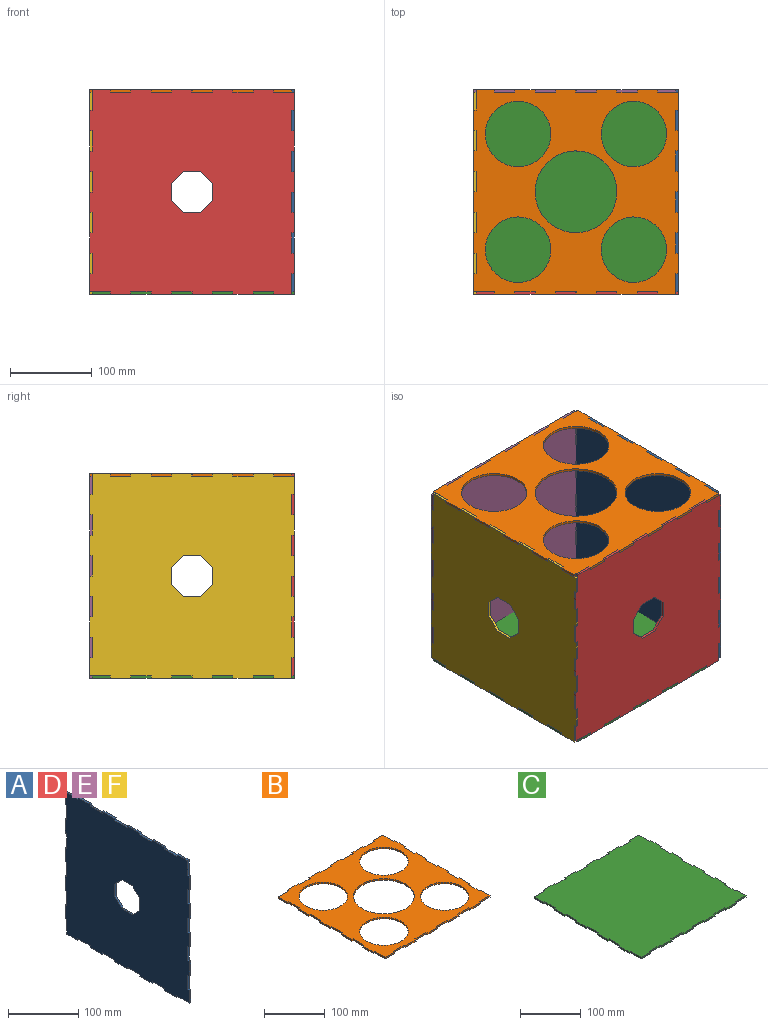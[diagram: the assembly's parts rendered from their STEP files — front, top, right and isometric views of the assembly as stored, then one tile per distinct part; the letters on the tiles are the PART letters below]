
ASSEMBLY  parts=6 mates=4
PART A: 86 faces, bbox 3x250x250 mm
  f0: plane 3x3mm, normal (0,0,1), area 9mm2, adj f1,f83,f84,f85
  f1: plane 25x3mm, normal (0,-1,0), area 75mm2, adj f0,f2,f84,f85
  f2: plane 3x3mm, normal (0,0,-1), area 9mm2, adj f1,f3,f84,f85
  f3: plane 25x3mm, normal (0,-1,0), area 75mm2, adj f2,f4,f84,f85
  f4: plane 3x3mm, normal (0,0,1), area 9mm2, adj f3,f5,f84,f85
  f5: plane 25x3mm, normal (0,-1,0), area 75mm2, adj f4,f6,f84,f85
  f6: plane 22x3mm, normal (0,0,1), area 66mm2, adj f5,f7,f84,f85
  f7: plane 3x3mm, normal (0,1,0), area 9mm2, adj f6,f8,f84,f85
  f8: plane 25x3mm, normal (0,0,1), area 75mm2, adj f7,f9,f84,f85
  f9: plane 3x3mm, normal (0,-1,0), area 9mm2, adj f8,f10,f84,f85
  f10: plane 25x3mm, normal (0,0,1), area 75mm2, adj f9,f11,f84,f85
  f11: plane 3x3mm, normal (0,1,0), area 9mm2, adj f10,f12,f84,f85
  f12: plane 25x3mm, normal (0,0,1), area 75mm2, adj f11,f13,f84,f85
  f13: plane 3x3mm, normal (0,-1,0), area 9mm2, adj f12,f14,f84,f85
  f14: plane 25x3mm, normal (0,0,1), area 75mm2, adj f13,f15,f84,f85
  f15: plane 3x3mm, normal (0,1,0), area 9mm2, adj f14,f16,f84,f85
  f16: plane 25x3mm, normal (0,0,1), area 75mm2, adj f15,f17,f84,f85
  f17: plane 3x3mm, normal (0,-1,0), area 9mm2, adj f16,f18,f84,f85
  f18: plane 25x3mm, normal (0,0,1), area 75mm2, adj f17,f19,f84,f85
  f19: plane 3x3mm, normal (0,1,0), area 9mm2, adj f18,f20,f84,f85
  f20: plane 25x3mm, normal (0,0,1), area 75mm2, adj f19,f21,f84,f85
  f21: plane 3x3mm, normal (0,-1,0), area 9mm2, adj f20,f22,f84,f85
  f22: plane 25x3mm, normal (0,0,1), area 75mm2, adj f21,f23,f84,f85
  f23: plane 3x3mm, normal (0,1,0), area 9mm2, adj f22,f24,f84,f85
  f24: plane 25x3mm, normal (0,0,1), area 75mm2, adj f23,f25,f84,f85
  f25: plane 22x3mm, normal (0,1,0), area 66mm2, adj f24,f26,f84,f85
  f26: plane 3x3mm, normal (0,0,-1), area 9mm2, adj f25,f27,f84,f85
  f27: plane 25x3mm, normal (0,1,0), area 75mm2, adj f26,f28,f84,f85
  f28: plane 3x3mm, normal (0,0,1), area 9mm2, adj f27,f29,f84,f85
  f29: plane 25x3mm, normal (0,1,0), area 75mm2, adj f28,f30,f84,f85
  f30: plane 3x3mm, normal (0,0,-1), area 9mm2, adj f29,f31,f84,f85
  f31: plane 25x3mm, normal (0,1,0), area 75mm2, adj f30,f32,f84,f85
  f32: plane 3x3mm, normal (0,0,1), area 9mm2, adj f31,f33,f84,f85
  f33: plane 25x3mm, normal (0,1,0), area 75mm2, adj f32,f34,f84,f85
  f34: plane 3x3mm, normal (0,0,-1), area 9mm2, adj f33,f35,f84,f85
  f35: plane 25x3mm, normal (0,1,0), area 75mm2, adj f34,f36,f84,f85
  f36: plane 3x3mm, normal (0,0,1), area 9mm2, adj f35,f37,f84,f85
  f37: plane 25x3mm, normal (0,1,0), area 75mm2, adj f36,f38,f84,f85
  f38: plane 3x3mm, normal (0,0,-1), area 9mm2, adj f37,f39,f84,f85
  f39: plane 25x3mm, normal (0,1,0), area 75mm2, adj f38,f40,f84,f85
  f40: plane 3x3mm, normal (0,0,1), area 9mm2, adj f39,f41,f84,f85
  f41: plane 25x3mm, normal (0,1,0), area 75mm2, adj f40,f42,f84,f85
  f42: plane 3x3mm, normal (0,0,-1), area 9mm2, adj f41,f43,f84,f85
  f43: plane 25x3mm, normal (0,1,0), area 75mm2, adj f42,f44,f84,f85
  f44: plane 22x3mm, normal (0,0,-1), area 66mm2, adj f43,f45,f84,f85
  f45: plane 3x3mm, normal (0,-1,0), area 9mm2, adj f44,f46,f84,f85
  f46: plane 25x3mm, normal (0,0,-1), area 75mm2, adj f45,f47,f84,f85
  f47: plane 3x3mm, normal (0,1,0), area 9mm2, adj f46,f48,f84,f85
  f48: plane 25x3mm, normal (0,0,-1), area 75mm2, adj f47,f49,f84,f85
  f49: plane 3x3mm, normal (0,-1,0), area 9mm2, adj f48,f50,f84,f85
  f50: plane 25x3mm, normal (0,0,-1), area 75mm2, adj f49,f51,f84,f85
  f51: plane 3x3mm, normal (0,1,0), area 9mm2, adj f50,f52,f84,f85
  f52: plane 25x3mm, normal (0,0,-1), area 75mm2, adj f51,f53,f84,f85
  f53: plane 3x3mm, normal (0,-1,0), area 9mm2, adj f52,f54,f84,f85
  f54: plane 25x3mm, normal (0,0,-1), area 75mm2, adj f53,f55,f84,f85
  f55: plane 3x3mm, normal (0,1,0), area 9mm2, adj f54,f56,f84,f85
  f56: plane 25x3mm, normal (0,0,-1), area 75mm2, adj f55,f57,f84,f85
  f57: plane 3x3mm, normal (0,-1,0), area 9mm2, adj f56,f58,f84,f85
  f58: plane 25x3mm, normal (0,0,-1), area 75mm2, adj f57,f59,f84,f85
  f59: plane 3x3mm, normal (0,1,0), area 9mm2, adj f58,f60,f84,f85
  f60: plane 25x3mm, normal (0,0,-1), area 75mm2, adj f59,f61,f84,f85
  f61: plane 3x3mm, normal (0,-1,0), area 9mm2, adj f60,f62,f84,f85
  f62: plane 25x3mm, normal (0,0,-1), area 75mm2, adj f61,f63,f84,f85
  f63: plane 22x3mm, normal (0,-1,0), area 66mm2, adj f62,f64,f84,f85
  f64: plane 3x3mm, normal (0,0,1), area 9mm2, adj f63,f65,f84,f85
  f65: plane 25x3mm, normal (0,-1,0), area 75mm2, adj f64,f66,f84,f85
  f66: plane 3x3mm, normal (0,0,-1), area 9mm2, adj f65,f67,f84,f85
  f67: plane 25x3mm, normal (0,-1,0), area 75mm2, adj f66,f68,f84,f85
  f68: plane 3x3mm, normal (0,0,1), area 9mm2, adj f67,f69,f84,f85
  f69: plane 25x3mm, normal (0,-1,0), area 75mm2, adj f68,f70,f84,f85
  f70: plane 3x3mm, normal (0,0,-1), area 9mm2, adj f69,f71,f84,f85
  f71: plane 25x3mm, normal (0,-1,0), area 75mm2, adj f70,f72,f84,f85
  f72: plane 3x3mm, normal (0,0,1), area 9mm2, adj f71,f73,f84,f85
  f73: plane 25x3mm, normal (0,-1,0), area 75mm2, adj f72,f74,f84,f85
  f74: plane 3x3mm, normal (0,0,-1), area 9mm2, adj f73,f83,f84,f85
  f75: plane 14.88x14.88mm, normal (0,-0.71,0.71), area 63.1mm2, adj f76,f82,f84,f85
  f76: plane 21.04x3mm, normal (0,-1,0), area 63.1mm2, adj f75,f77,f84,f85
  f77: plane 14.88x14.88mm, normal (0,-0.71,-0.71), area 63.1mm2, adj f76,f78,f84,f85
  f78: plane 21.04x3mm, normal (0,0,-1), area 63.1mm2, adj f77,f79,f84,f85
  f79: plane 14.88x14.88mm, normal (0,0.71,-0.71), area 63.1mm2, adj f78,f80,f84,f85
  f80: plane 21.04x3mm, normal (0,1,0), area 63.1mm2, adj f79,f81,f84,f85
  f81: plane 14.88x14.88mm, normal (0,0.71,0.71), area 63.1mm2, adj f80,f82,f84,f85
  f82: plane 21.04x3mm, normal (0,0,1), area 63.1mm2, adj f75,f81,f84,f85
  f83: plane 25x3mm, normal (0,-1,0), area 75mm2, adj f0,f74,f84,f85
  f84: plane 250x250mm, normal (-1,0,0), area 58862.1mm2, adj f0,f1,f2,f3,f4,f5,f6,f7
  f85: plane 250x250mm, normal (1,0,0), area 58862.1mm2, adj f0,f1,f2,f3,f4,f5,f6,f7
PART B: 83 faces, bbox 250x250x3 mm
  f0: plane 3x3mm, normal (0,1,0), area 9mm2, adj f1,f80,f81,f82
  f1: plane 25x3mm, normal (1,0,0), area 75mm2, adj f0,f2,f81,f82
  f2: plane 3x3mm, normal (0,-1,0), area 9mm2, adj f1,f3,f81,f82
  f3: plane 25x3mm, normal (1,0,0), area 75mm2, adj f2,f4,f81,f82
  f4: plane 3x3mm, normal (0,1,0), area 9mm2, adj f3,f5,f81,f82
  f5: plane 25x3mm, normal (1,0,0), area 75mm2, adj f4,f6,f81,f82
  f6: plane 22x3mm, normal (0,1,0), area 66mm2, adj f5,f7,f81,f82
  f7: plane 3x3mm, normal (-1,0,0), area 9mm2, adj f6,f8,f81,f82
  f8: plane 25x3mm, normal (0,1,0), area 75mm2, adj f7,f9,f81,f82
  f9: plane 3x3mm, normal (1,0,0), area 9mm2, adj f8,f10,f81,f82
  f10: plane 25x3mm, normal (0,1,0), area 75mm2, adj f9,f11,f81,f82
  f11: plane 3x3mm, normal (-1,0,0), area 9mm2, adj f10,f12,f81,f82
  f12: plane 25x3mm, normal (0,1,0), area 75mm2, adj f11,f13,f81,f82
  f13: plane 3x3mm, normal (1,0,0), area 9mm2, adj f12,f14,f81,f82
  f14: plane 25x3mm, normal (0,1,0), area 75mm2, adj f13,f15,f81,f82
  f15: plane 3x3mm, normal (-1,0,0), area 9mm2, adj f14,f16,f81,f82
  f16: plane 25x3mm, normal (0,1,0), area 75mm2, adj f15,f17,f81,f82
  f17: plane 3x3mm, normal (1,0,0), area 9mm2, adj f16,f18,f81,f82
  f18: plane 25x3mm, normal (0,1,0), area 75mm2, adj f17,f19,f81,f82
  f19: plane 3x3mm, normal (-1,0,0), area 9mm2, adj f18,f20,f81,f82
  f20: plane 25x3mm, normal (0,1,0), area 75mm2, adj f19,f21,f81,f82
  f21: plane 3x3mm, normal (1,0,0), area 9mm2, adj f20,f22,f81,f82
  f22: plane 25x3mm, normal (0,1,0), area 75mm2, adj f21,f23,f81,f82
  f23: plane 3x3mm, normal (-1,0,0), area 9mm2, adj f22,f24,f81,f82
  f24: plane 25x3mm, normal (0,1,0), area 75mm2, adj f23,f25,f81,f82
  f25: plane 22x3mm, normal (-1,0,0), area 66mm2, adj f24,f26,f81,f82
  f26: plane 3x3mm, normal (0,-1,0), area 9mm2, adj f25,f27,f81,f82
  f27: plane 25x3mm, normal (-1,0,0), area 75mm2, adj f26,f28,f81,f82
  f28: plane 3x3mm, normal (0,1,0), area 9mm2, adj f27,f29,f81,f82
  f29: plane 25x3mm, normal (-1,0,0), area 75mm2, adj f28,f30,f81,f82
  f30: plane 3x3mm, normal (0,-1,0), area 9mm2, adj f29,f31,f81,f82
  f31: plane 25x3mm, normal (-1,0,0), area 75mm2, adj f30,f32,f81,f82
  f32: plane 3x3mm, normal (0,1,0), area 9mm2, adj f31,f33,f81,f82
  f33: plane 25x3mm, normal (-1,0,0), area 75mm2, adj f32,f34,f81,f82
  f34: plane 3x3mm, normal (0,-1,0), area 9mm2, adj f33,f35,f81,f82
  f35: plane 25x3mm, normal (-1,0,0), area 75mm2, adj f34,f36,f81,f82
  f36: plane 3x3mm, normal (0,1,0), area 9mm2, adj f35,f37,f81,f82
  f37: plane 25x3mm, normal (-1,0,0), area 75mm2, adj f36,f38,f81,f82
  f38: plane 3x3mm, normal (0,-1,0), area 9mm2, adj f37,f39,f81,f82
  f39: plane 25x3mm, normal (-1,0,0), area 75mm2, adj f38,f40,f81,f82
  f40: plane 3x3mm, normal (0,1,0), area 9mm2, adj f39,f41,f81,f82
  f41: plane 25x3mm, normal (-1,0,0), area 75mm2, adj f40,f42,f81,f82
  f42: plane 3x3mm, normal (0,-1,0), area 9mm2, adj f41,f43,f81,f82
  f43: plane 25x3mm, normal (-1,0,0), area 75mm2, adj f42,f44,f81,f82
  f44: plane 22x3mm, normal (0,-1,0), area 66mm2, adj f43,f45,f81,f82
  f45: plane 3x3mm, normal (1,0,0), area 9mm2, adj f44,f46,f81,f82
  f46: plane 25x3mm, normal (0,-1,0), area 75mm2, adj f45,f47,f81,f82
  f47: plane 3x3mm, normal (-1,0,0), area 9mm2, adj f46,f48,f81,f82
  f48: plane 25x3mm, normal (0,-1,0), area 75mm2, adj f47,f49,f81,f82
  f49: plane 3x3mm, normal (1,0,0), area 9mm2, adj f48,f50,f81,f82
  f50: plane 25x3mm, normal (0,-1,0), area 75mm2, adj f49,f51,f81,f82
  f51: plane 3x3mm, normal (-1,0,0), area 9mm2, adj f50,f52,f81,f82
  f52: plane 25x3mm, normal (0,-1,0), area 75mm2, adj f51,f53,f81,f82
  f53: plane 3x3mm, normal (1,0,0), area 9mm2, adj f52,f54,f81,f82
  f54: plane 25x3mm, normal (0,-1,0), area 75mm2, adj f53,f55,f81,f82
  f55: plane 3x3mm, normal (-1,0,0), area 9mm2, adj f54,f56,f81,f82
  f56: plane 25x3mm, normal (0,-1,0), area 75mm2, adj f55,f57,f81,f82
  f57: plane 3x3mm, normal (1,0,0), area 9mm2, adj f56,f58,f81,f82
  f58: plane 25x3mm, normal (0,-1,0), area 75mm2, adj f57,f59,f81,f82
  f59: plane 3x3mm, normal (-1,0,0), area 9mm2, adj f58,f60,f81,f82
  f60: plane 25x3mm, normal (0,-1,0), area 75mm2, adj f59,f61,f81,f82
  f61: plane 3x3mm, normal (1,0,0), area 9mm2, adj f60,f62,f81,f82
  f62: plane 25x3mm, normal (0,-1,0), area 75mm2, adj f61,f63,f81,f82
  f63: plane 22x3mm, normal (1,0,0), area 66mm2, adj f62,f64,f81,f82
  f64: plane 3x3mm, normal (0,1,0), area 9mm2, adj f63,f65,f81,f82
  f65: plane 25x3mm, normal (1,0,0), area 75mm2, adj f64,f66,f81,f82
  f66: plane 3x3mm, normal (0,-1,0), area 9mm2, adj f65,f67,f81,f82
  f67: plane 25x3mm, normal (1,0,0), area 75mm2, adj f66,f68,f81,f82
  f68: plane 3x3mm, normal (0,1,0), area 9mm2, adj f67,f69,f81,f82
  f69: plane 25x3mm, normal (1,0,0), area 75mm2, adj f68,f70,f81,f82
  f70: plane 3x3mm, normal (0,-1,0), area 9mm2, adj f69,f71,f81,f82
  f71: plane 25x3mm, normal (1,0,0), area 75mm2, adj f70,f72,f81,f82
  f72: plane 3x3mm, normal (0,1,0), area 9mm2, adj f71,f73,f81,f82
  f73: plane 25x3mm, normal (1,0,0), area 75mm2, adj f72,f74,f81,f82
  f74: plane 3x3mm, normal (0,-1,0), area 9mm2, adj f73,f80,f81,f82
  f75: cylinder r=40mm len=80mm, axis (0,0,1), area 754mm2, adj f81,f82
  f76: cylinder r=40mm len=80mm, axis (0,0,1), area 754mm2, adj f81,f82
  f77: cylinder r=40mm len=80mm, axis (0,0,1), area 754mm2, adj f81,f82
  f78: cylinder r=40mm len=80mm, axis (0,0,1), area 754mm2, adj f81,f82
  f79: cylinder r=50mm len=100mm, axis (0,0,1), area 942.5mm2, adj f81,f82
  f80: plane 25x3mm, normal (1,0,0), area 75mm2, adj f0,f74,f81,f82
  f81: plane 250x250mm, normal (0,0,1), area 33039.8mm2, adj f0,f1,f2,f3,f4,f5,f6,f7
  f82: plane 250x250mm, normal (0,0,-1), area 33039.8mm2, adj f0,f1,f2,f3,f4,f5,f6,f7
PART C: 78 faces, bbox 250x250x3 mm
  f0: plane 3x3mm, normal (0,1,0), area 9mm2, adj f1,f75,f76,f77
  f1: plane 25x3mm, normal (1,0,0), area 75mm2, adj f0,f2,f76,f77
  f2: plane 3x3mm, normal (0,-1,0), area 9mm2, adj f1,f3,f76,f77
  f3: plane 25x3mm, normal (1,0,0), area 75mm2, adj f2,f4,f76,f77
  f4: plane 3x3mm, normal (0,1,0), area 9mm2, adj f3,f5,f76,f77
  f5: plane 25x3mm, normal (1,0,0), area 75mm2, adj f4,f6,f76,f77
  f6: plane 22x3mm, normal (0,1,0), area 66mm2, adj f5,f7,f76,f77
  f7: plane 3x3mm, normal (-1,0,0), area 9mm2, adj f6,f8,f76,f77
  f8: plane 25x3mm, normal (0,1,0), area 75mm2, adj f7,f9,f76,f77
  f9: plane 3x3mm, normal (1,0,0), area 9mm2, adj f8,f10,f76,f77
  f10: plane 25x3mm, normal (0,1,0), area 75mm2, adj f9,f11,f76,f77
  f11: plane 3x3mm, normal (-1,0,0), area 9mm2, adj f10,f12,f76,f77
  f12: plane 25x3mm, normal (0,1,0), area 75mm2, adj f11,f13,f76,f77
  f13: plane 3x3mm, normal (1,0,0), area 9mm2, adj f12,f14,f76,f77
  f14: plane 25x3mm, normal (0,1,0), area 75mm2, adj f13,f15,f76,f77
  f15: plane 3x3mm, normal (-1,0,0), area 9mm2, adj f14,f16,f76,f77
  f16: plane 25x3mm, normal (0,1,0), area 75mm2, adj f15,f17,f76,f77
  f17: plane 3x3mm, normal (1,0,0), area 9mm2, adj f16,f18,f76,f77
  f18: plane 25x3mm, normal (0,1,0), area 75mm2, adj f17,f19,f76,f77
  f19: plane 3x3mm, normal (-1,0,0), area 9mm2, adj f18,f20,f76,f77
  f20: plane 25x3mm, normal (0,1,0), area 75mm2, adj f19,f21,f76,f77
  f21: plane 3x3mm, normal (1,0,0), area 9mm2, adj f20,f22,f76,f77
  f22: plane 25x3mm, normal (0,1,0), area 75mm2, adj f21,f23,f76,f77
  f23: plane 3x3mm, normal (-1,0,0), area 9mm2, adj f22,f24,f76,f77
  f24: plane 25x3mm, normal (0,1,0), area 75mm2, adj f23,f25,f76,f77
  f25: plane 22x3mm, normal (-1,0,0), area 66mm2, adj f24,f26,f76,f77
  f26: plane 3x3mm, normal (0,-1,0), area 9mm2, adj f25,f27,f76,f77
  f27: plane 25x3mm, normal (-1,0,0), area 75mm2, adj f26,f28,f76,f77
  f28: plane 3x3mm, normal (0,1,0), area 9mm2, adj f27,f29,f76,f77
  f29: plane 25x3mm, normal (-1,0,0), area 75mm2, adj f28,f30,f76,f77
  f30: plane 3x3mm, normal (0,-1,0), area 9mm2, adj f29,f31,f76,f77
  f31: plane 25x3mm, normal (-1,0,0), area 75mm2, adj f30,f32,f76,f77
  f32: plane 3x3mm, normal (0,1,0), area 9mm2, adj f31,f33,f76,f77
  f33: plane 25x3mm, normal (-1,0,0), area 75mm2, adj f32,f34,f76,f77
  f34: plane 3x3mm, normal (0,-1,0), area 9mm2, adj f33,f35,f76,f77
  f35: plane 25x3mm, normal (-1,0,0), area 75mm2, adj f34,f36,f76,f77
  f36: plane 3x3mm, normal (0,1,0), area 9mm2, adj f35,f37,f76,f77
  f37: plane 25x3mm, normal (-1,0,0), area 75mm2, adj f36,f38,f76,f77
  f38: plane 3x3mm, normal (0,-1,0), area 9mm2, adj f37,f39,f76,f77
  f39: plane 25x3mm, normal (-1,0,0), area 75mm2, adj f38,f40,f76,f77
  f40: plane 3x3mm, normal (0,1,0), area 9mm2, adj f39,f41,f76,f77
  f41: plane 25x3mm, normal (-1,0,0), area 75mm2, adj f40,f42,f76,f77
  f42: plane 3x3mm, normal (0,-1,0), area 9mm2, adj f41,f43,f76,f77
  f43: plane 25x3mm, normal (-1,0,0), area 75mm2, adj f42,f44,f76,f77
  f44: plane 22x3mm, normal (0,-1,0), area 66mm2, adj f43,f45,f76,f77
  f45: plane 3x3mm, normal (1,0,0), area 9mm2, adj f44,f46,f76,f77
  f46: plane 25x3mm, normal (0,-1,0), area 75mm2, adj f45,f47,f76,f77
  f47: plane 3x3mm, normal (-1,0,0), area 9mm2, adj f46,f48,f76,f77
  f48: plane 25x3mm, normal (0,-1,0), area 75mm2, adj f47,f49,f76,f77
  f49: plane 3x3mm, normal (1,0,0), area 9mm2, adj f48,f50,f76,f77
  f50: plane 25x3mm, normal (0,-1,0), area 75mm2, adj f49,f51,f76,f77
  f51: plane 3x3mm, normal (-1,0,0), area 9mm2, adj f50,f52,f76,f77
  f52: plane 25x3mm, normal (0,-1,0), area 75mm2, adj f51,f53,f76,f77
  f53: plane 3x3mm, normal (1,0,0), area 9mm2, adj f52,f54,f76,f77
  f54: plane 25x3mm, normal (0,-1,0), area 75mm2, adj f53,f55,f76,f77
  f55: plane 3x3mm, normal (-1,0,0), area 9mm2, adj f54,f56,f76,f77
  f56: plane 25x3mm, normal (0,-1,0), area 75mm2, adj f55,f57,f76,f77
  f57: plane 3x3mm, normal (1,0,0), area 9mm2, adj f56,f58,f76,f77
  f58: plane 25x3mm, normal (0,-1,0), area 75mm2, adj f57,f59,f76,f77
  f59: plane 3x3mm, normal (-1,0,0), area 9mm2, adj f58,f60,f76,f77
  f60: plane 25x3mm, normal (0,-1,0), area 75mm2, adj f59,f61,f76,f77
  f61: plane 3x3mm, normal (1,0,0), area 9mm2, adj f60,f62,f76,f77
  f62: plane 25x3mm, normal (0,-1,0), area 75mm2, adj f61,f63,f76,f77
  f63: plane 22x3mm, normal (1,0,0), area 66mm2, adj f62,f64,f76,f77
  f64: plane 3x3mm, normal (0,1,0), area 9mm2, adj f63,f65,f76,f77
  f65: plane 25x3mm, normal (1,0,0), area 75mm2, adj f64,f66,f76,f77
  f66: plane 3x3mm, normal (0,-1,0), area 9mm2, adj f65,f67,f76,f77
  f67: plane 25x3mm, normal (1,0,0), area 75mm2, adj f66,f68,f76,f77
  f68: plane 3x3mm, normal (0,1,0), area 9mm2, adj f67,f69,f76,f77
  f69: plane 25x3mm, normal (1,0,0), area 75mm2, adj f68,f70,f76,f77
  f70: plane 3x3mm, normal (0,-1,0), area 9mm2, adj f69,f71,f76,f77
  f71: plane 25x3mm, normal (1,0,0), area 75mm2, adj f70,f72,f76,f77
  f72: plane 3x3mm, normal (0,1,0), area 9mm2, adj f71,f73,f76,f77
  f73: plane 25x3mm, normal (1,0,0), area 75mm2, adj f72,f74,f76,f77
  f74: plane 3x3mm, normal (0,-1,0), area 9mm2, adj f73,f75,f76,f77
  f75: plane 25x3mm, normal (1,0,0), area 75mm2, adj f0,f74,f76,f77
  f76: plane 250x250mm, normal (0,0,1), area 61000mm2, adj f0,f1,f2,f3,f4,f5,f6,f7
  f77: plane 250x250mm, normal (0,0,-1), area 61000mm2, adj f0,f1,f2,f3,f4,f5,f6,f7
PART D: same geometry as A
PART E: same geometry as A
PART F: same geometry as A
PLACE A t=(244,247,4.5)mm
PLACE B rot(axis=(1,0,0),180deg) t=(0,0,248.5)mm
PLACE C t=(0,0,1.5)mm
PLACE D rot(axis=(0,0,-1),90deg) t=(247,-244,4.5)mm
PLACE E rot(axis=(0,0,1),90deg) t=(-247,244,4.5)mm
PLACE F rot(axis=(0,0,1),180deg) t=(-244,-247,4.5)mm
MATE planar A.f44 <-> C.f77  axis (0,0,-1) through (123.5,111,0)mm
MATE planar A.f41 <-> C.f6  axis (0,1,0) through (123.5,125,37.5)mm
MATE planar B.f79 <-> A.f24  axis (0,0,-1) through (0,0,247)mm
MATE planar A.f85 <-> C.f3  axis (1,0,0) through (125,0,125)mm
